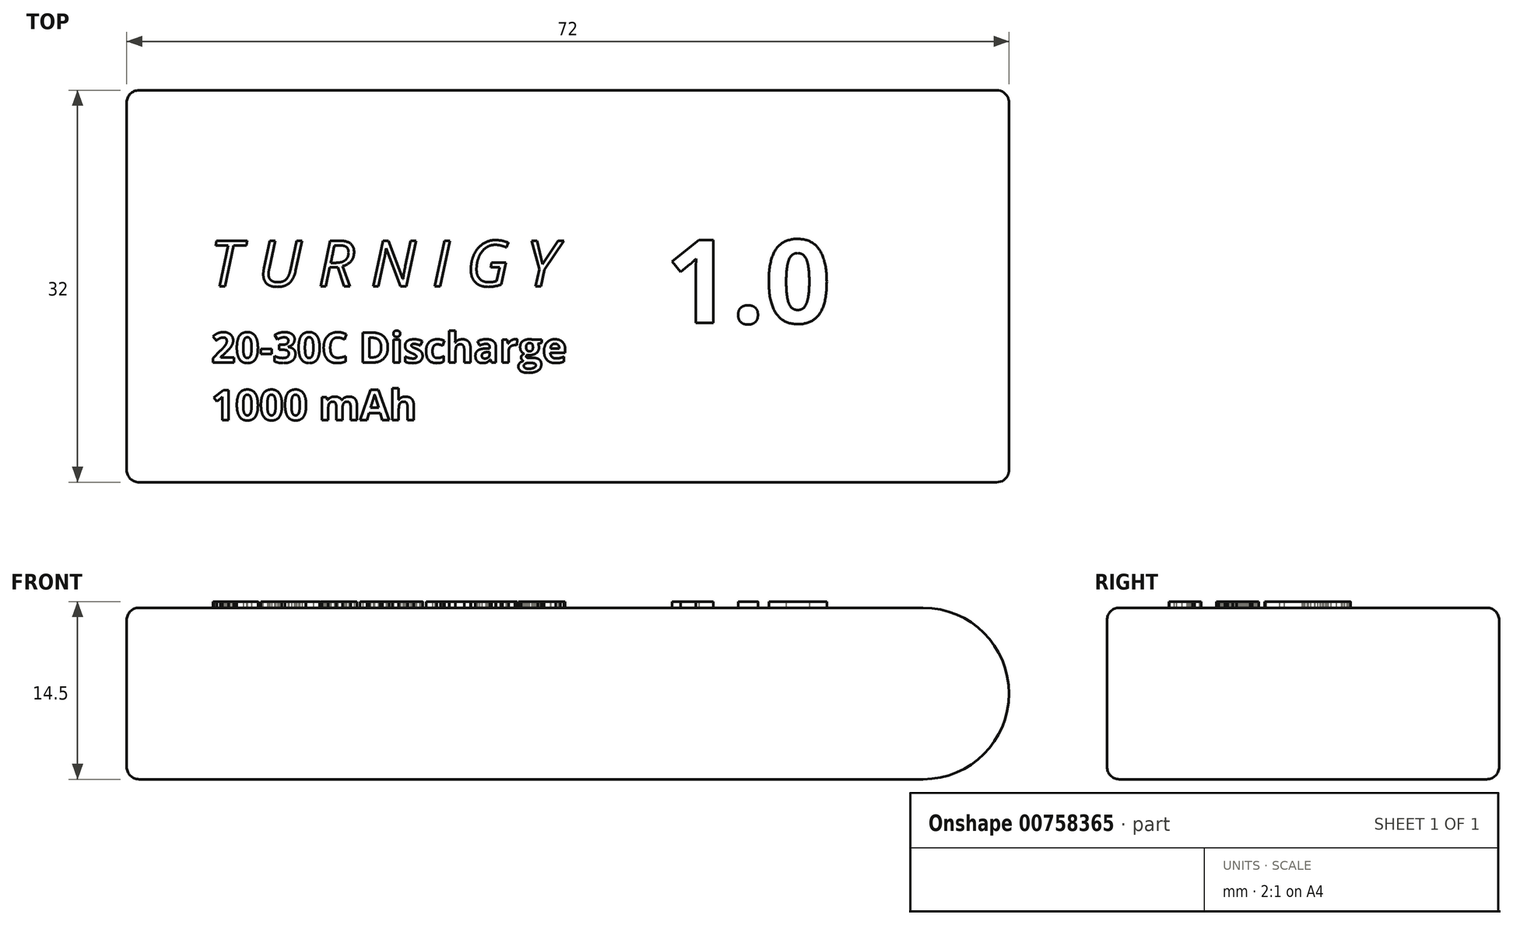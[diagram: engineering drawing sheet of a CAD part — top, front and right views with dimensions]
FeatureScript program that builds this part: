
annotation { "Feature Type Name" : "Feature", "Feature Type Description" : "" }
export const myFeature = defineFeature(function(context is Context, id is Id, definition is map)
    precondition{}
    {
        {
            var Q0;
            Q0=qCreatedBy(makeId("Front.planeOp"),FACE);
            var sketch = newSketch(context, id + "F0", { "sketchPlane" : qUnion([Q0])});
            skLineSegment(sketch, "E0.bottom", {"start": v(36, 7) * mm, "end": v(-36, 7) * mm});
            skLineSegment(sketch, "E0.top", {"start": v(36, -7) * mm, "end": v(-36, -7) * mm});
            skLineSegment(sketch, "E0.left", {"start": v(36, 7) * mm, "end": v(36, -7) * mm});
            skLineSegment(sketch, "E0.right", {"start": v(-36, 7) * mm, "end": v(-36, -7) * mm});
            skPoint(sketch, "E0.middle", {"position": v(0, 0) * mm});
            skSolve(sketch);
        }
        {
            var Q0;
            Q0=makeQuery(id+"F0.imprint","IMPRINT",FACE,{"disambiguationData":[TD([[makeQuery(id+"F0.imprint","IMPRINT",EDGE,{"derivedFrom":sQuery(id+"F0.wireOp",EDGE,"E0.bottom")}),1.0]])]});
            extrude(context, id + "F1", {"entities" : qUnion([Q0]), "endBound" : BoundingType.SYMMETRIC, "depth" : 32 * mm});
        }
        {
            var Q0;
            Q0=makeQuery(id+"F1.opExtrude","SWEPT_EDGE",EDGE,{"disambiguationData":[OSD([sQuery(id+"F0.wireOp",EDGE,"E0.bottom"),sQuery(id+"F0.wireOp",EDGE,"E0.left")])]});
            var Q1;
            Q1=makeQuery(id+"F1.opExtrude","SWEPT_EDGE",EDGE,{"disambiguationData":[OSD([sQuery(id+"F0.wireOp",EDGE,"E0.top"),sQuery(id+"F0.wireOp",EDGE,"E0.left")])]});
            fillet(context, id + "F2", {"entities" : qUnion([Q0, Q1]), "radius" : 7 * mm, "tangentPropagation" : true, "allowEdgeOverflow" : false});
        }
        {
            var Q0;
            Q0=makeQuery(id+"F1.opExtrude","CAP_EDGE",EDGE,{"disambiguationData":[OSD([sQuery(id+"F0.wireOp",EDGE,"E0.bottom")])],"isStart":false});
            var Q1;
            Q1=makeQuery(id+"F1.opExtrude","CAP_EDGE",EDGE,{"disambiguationData":[OSD([sQuery(id+"F0.wireOp",EDGE,"E0.bottom")])],"isStart":true});
            var Q2;
            Q2=makeQuery(id+"F1.opExtrude","SWEPT_EDGE",EDGE,{"disambiguationData":[OSD([sQuery(id+"F0.wireOp",EDGE,"E0.top"),sQuery(id+"F0.wireOp",EDGE,"E0.right")])]});
            var Q3;
            Q3=makeQuery(id+"F1.opExtrude","CAP_EDGE",EDGE,{"disambiguationData":[OSD([sQuery(id+"F0.wireOp",EDGE,"E0.right")])],"isStart":true});
            var Q4;
            Q4=makeQuery(id+"F1.opExtrude","CAP_EDGE",EDGE,{"disambiguationData":[OSD([sQuery(id+"F0.wireOp",EDGE,"E0.right")])],"isStart":false});
            fillet(context, id + "F3", {"entities" : qUnion([Q0, Q1, Q2, Q3, Q4]), "radius" : 1 * mm, "tangentPropagation" : true, "allowEdgeOverflow" : false});
        }
        {
            var Q0;
            Q0=makeQuery(id+"F1.opExtrude","SWEPT_EDGE",EDGE,{"disambiguationData":[OSD([sQuery(id+"F0.wireOp",EDGE,"E0.bottom"),sQuery(id+"F0.wireOp",EDGE,"E0.right")])]});
            fillet(context, id + "F4", {"entities" : qUnion([Q0]), "radius" : 1 * mm, "tangentPropagation" : true, "allowEdgeOverflow" : false});
        }
        {
            var Q0;
            Q0=makeQuery(id+"F1.opExtrude","SWEPT_FACE",FACE,{"disambiguationData":[OSD([sQuery(id+"F0.wireOp",EDGE,"E0.bottom")])]});
            var sketch = newSketch(context, id + "F5", { "sketchPlane" : qUnion([Q0])});
            skText(sketch, "E1", { "text": "T U R N I G Y", "fontName": "OpenSans-Italic.ttf"});
            skText(sketch, "E2", { "text": "20-30C Discharge\n1000 mAh", "fontName": "OpenSans-Bold.ttf"});
            skText(sketch, "E3", { "text": "1.0", "fontName": "OpenSans-Bold.ttf"});
            const initialGuessF5  = {"E1": [-0.02922, 0, 1, 0, 0.00375], "E2": [-0.0291, -0.00624, 1, 0, 0.00248], "E3": [0.00795, -0.003, 1, 0, 0.00682]};
            skSetInitialGuess(sketch, initialGuessF5);
            skSolve(sketch);
        }
        {
            var Q0;
            Q0=qSketchRegion(id+"F5",true);
            extrude(context, id + "F6", {"entities" : qUnion([Q0]), "operationType" : NewBodyOperationType.ADD, "depth" : .5 * mm});
        }
    });
